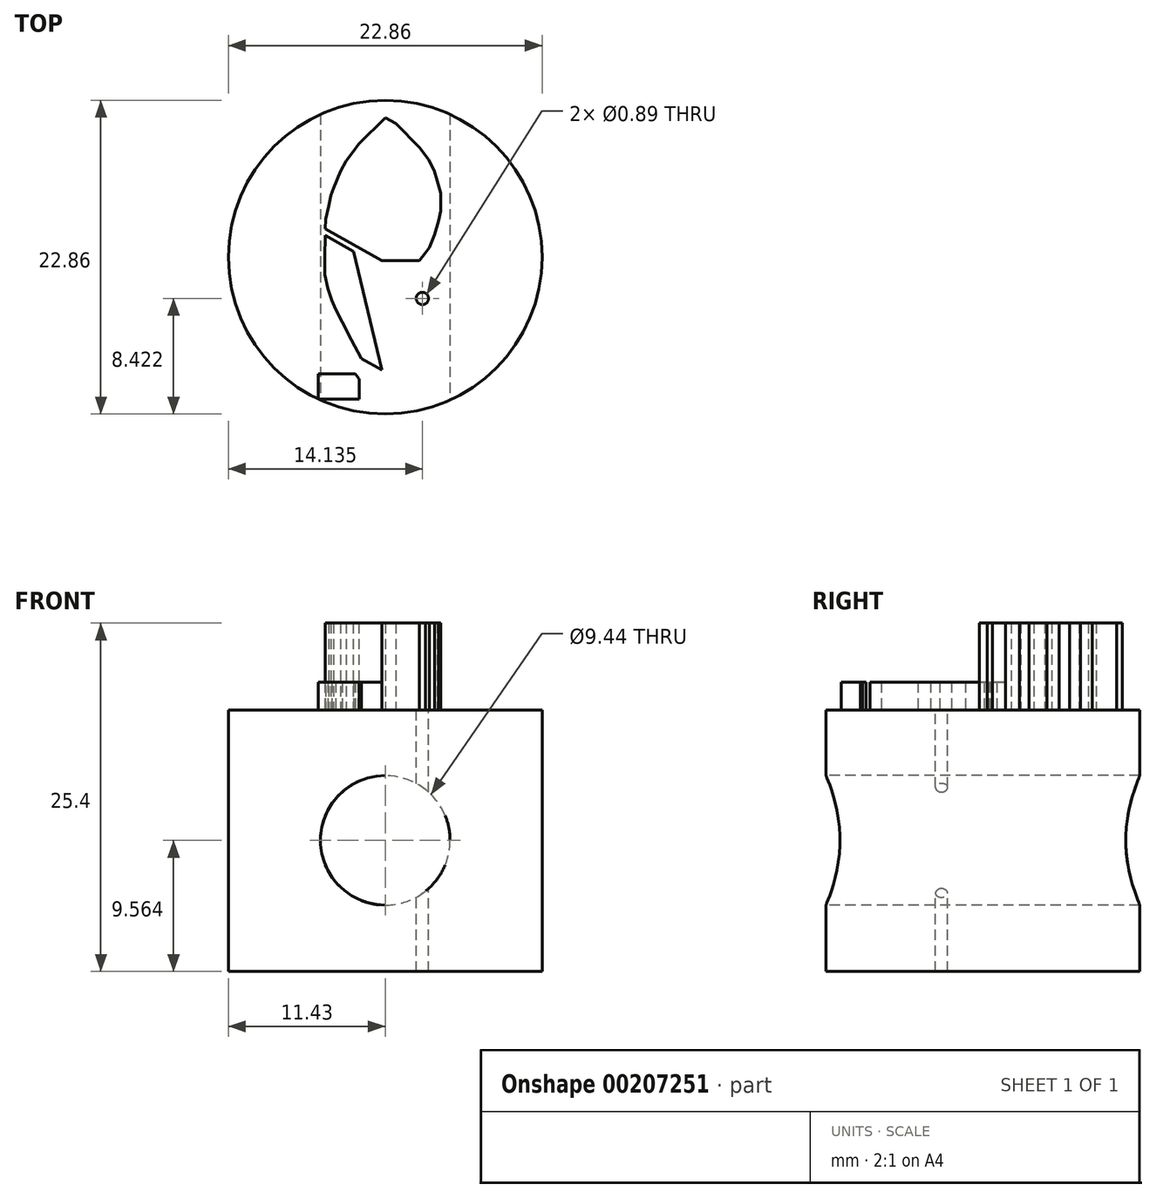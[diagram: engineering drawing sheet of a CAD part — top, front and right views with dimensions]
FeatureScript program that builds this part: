
annotation { "Feature Type Name" : "Feature", "Feature Type Description" : "" }
export const myFeature = defineFeature(function(context is Context, id is Id, definition is map)
    precondition{}
    {
        {
            var Q0;
            Q0=qCreatedBy(makeId("Top.planeOp"),FACE);
            var sketch = newSketch(context, id + "F0", { "sketchPlane" : qUnion([Q0])});
            skCircle(sketch, "E0", {"center": v(0, 0) * mm, "radius": 11.43 * mm});
            skSolve(sketch);
        }
        {
            var Q0;
            Q0 = qSketchRegion(id + "F0", true);
            extrude(context, id + "F1", {"entities" : qUnion([Q0]), "depth" : 19.05 * mm});
        }
        {
            var Q0;
            Q0=makeQuery(id+"F1.opExtrude","CAP_FACE",FACE,{"disambiguationData":[OSD([sQuery(id+"F0.wireOp",EDGE,"E0")])],"isStart":false});
            var sketch = newSketch(context, id + "F2", { "sketchPlane" : qUnion([Q0])});
            skCircle(sketch, "E1", {"center": v(2.7, -3) * mm, "radius": 0.45 * mm});
            skSolve(sketch);
        }
        {
            var Q0;
            Q0 = qSketchRegion(id + "F2", true);
            extrude(context, id + "F3", {"entities" : qUnion([Q0]), "operationType" : NewBodyOperationType.REMOVE, "oppositeDirection" : true, "depth" : 19.06 * mm});
        }
        {
            var Q0;
            Q0=makeQuery(id+"F1.opExtrude","CAP_FACE",FACE,{"disambiguationData":[OSD([sQuery(id+"F0.wireOp",EDGE,"E0")])],"isStart":false});
            var sketch = newSketch(context, id + "F4", { "sketchPlane" : qUnion([Q0])});
            skLineSegment(sketch, "E2", {"start": v(-2.18, -8.51) * mm, "end": v(-1.98, -8.77) * mm});
            skLineSegment(sketch, "E3", {"start": v(-1.98, -8.77) * mm, "end": v(-1.93, -8.85) * mm});
            skLineSegment(sketch, "E4", {"start": v(-1.93, -8.85) * mm, "end": v(-1.88, -8.92) * mm});
            skLineSegment(sketch, "E5", {"start": v(-1.88, -8.92) * mm, "end": v(-1.88, -9.2) * mm});
            skLineSegment(sketch, "E6", {"start": v(-1.88, -9.2) * mm, "end": v(-1.88, -9.88) * mm});
            skLineSegment(sketch, "E7", {"start": v(-1.88, -9.88) * mm, "end": v(-1.88, -10.33) * mm});
            skLineSegment(sketch, "E8", {"start": v(-4.89, -10.33) * mm, "end": v(-4.89, -8.51) * mm});
            skLineSegment(sketch, "E9", {"start": v(-4.89, -8.51) * mm, "end": v(-2.18, -8.51) * mm});
            skLineSegment(sketch, "E10", {"start": v(-4.89, -10.33) * mm, "end": v(-1.88, -10.33) * mm});
            skSolve(sketch);
        }
        {
            var Q0;
            Q0 = qSketchRegion(id + "F4", true);
            extrude(context, id + "F5", {"entities" : qUnion([Q0]), "operationType" : NewBodyOperationType.ADD, "depth" : 2.03 * mm});
        }
        {
            var Q0;
            Q0=makeQuery(id+"F1.opExtrude","CAP_FACE",FACE,{"disambiguationData":[OSD([sQuery(id+"F0.wireOp",EDGE,"E0")])],"isStart":false});
            var sketch = newSketch(context, id + "F6", { "sketchPlane" : qUnion([Q0])});
            skLineSegment(sketch, "E11", {"start": v(4.03, 3.8) * mm, "end": v(4.03, 4.68) * mm});
            skLineSegment(sketch, "E12", {"start": v(4.03, 4.68) * mm, "end": v(3.8, 5.57) * mm});
            skLineSegment(sketch, "E13", {"start": v(3.8, 5.57) * mm, "end": v(3.57, 6.33) * mm});
            skLineSegment(sketch, "E14", {"start": v(3.57, 6.33) * mm, "end": v(3.15, 7.12) * mm});
            skLineSegment(sketch, "E15", {"start": v(3.15, 7.12) * mm, "end": v(2.5, 7.98) * mm});
            skLineSegment(sketch, "E16", {"start": v(2.5, 7.98) * mm, "end": v(1.66, 8.85) * mm});
            skLineSegment(sketch, "E17", {"start": v(1.66, 8.85) * mm, "end": v(1.2, 9.32) * mm});
            skLineSegment(sketch, "E18", {"start": v(1.2, 9.32) * mm, "end": v(0.78, 9.74) * mm});
            skLineSegment(sketch, "E19", {"start": v(0.78, 9.74) * mm, "end": v(0, 10.16) * mm});
            skLineSegment(sketch, "E20", {"start": v(0, 10.16) * mm, "end": v(-0.6, 9.56) * mm});
            skLineSegment(sketch, "E21", {"start": v(-0.6, 9.56) * mm, "end": v(-1.34, 8.85) * mm});
            skLineSegment(sketch, "E22", {"start": v(-1.34, 8.85) * mm, "end": v(-1.94, 8.26) * mm});
            skLineSegment(sketch, "E23", {"start": v(-1.94, 8.26) * mm, "end": v(-2.33, 7.68) * mm});
            skLineSegment(sketch, "E24", {"start": v(-3.15, -4.72) * mm, "end": v(-2.46, -6.03) * mm});
            skLineSegment(sketch, "E25", {"start": v(-2.46, -6.03) * mm, "end": v(-1.74, -7.4) * mm});
            skLineSegment(sketch, "E26", {"start": v(-1.74, -7.4) * mm, "end": v(-0.24, -8.21) * mm});
            skLineSegment(sketch, "E27", {"start": v(-4.38, 1.01) * mm, "end": v(-4.38, 1.57) * mm});
            skLineSegment(sketch, "E28", {"start": v(-4.1, 3.71) * mm, "end": v(-3.95, 4.5) * mm});
            skLineSegment(sketch, "E29", {"start": v(-3.95, 4.5) * mm, "end": v(-3.76, 5) * mm});
            skLineSegment(sketch, "E30", {"start": v(-3.76, 5) * mm, "end": v(-3.27, 6.25) * mm});
            skLineSegment(sketch, "E31", {"start": v(-3.27, 6.25) * mm, "end": v(-2.84, 7.02) * mm});
            skLineSegment(sketch, "E32", {"start": v(-2.84, 7.02) * mm, "end": v(-2.33, 7.68) * mm});
            skLineSegment(sketch, "E33", {"start": v(-4.38, 2.07) * mm, "end": v(-4.34, 2.75) * mm});
            skLineSegment(sketch, "E34", {"start": v(-4.34, 2.75) * mm, "end": v(-4.1, 3.71) * mm});
            skLineSegment(sketch, "E35", {"start": v(-4.42, -0.55) * mm, "end": v(-4.42, 0.1) * mm});
            skLineSegment(sketch, "E36", {"start": v(-4.42, 0.1) * mm, "end": v(-4.4, 0.53) * mm});
            skLineSegment(sketch, "E37", {"start": v(-4.4, 0.53) * mm, "end": v(-4.38, 1.01) * mm});
            skLineSegment(sketch, "E38", {"start": v(-3.15, -4.72) * mm, "end": v(-3.6, -3.81) * mm});
            skLineSegment(sketch, "E39", {"start": v(-3.6, -3.81) * mm, "end": v(-3.9, -3.14) * mm});
            skLineSegment(sketch, "E40", {"start": v(-3.9, -3.14) * mm, "end": v(-4.18, -2.3) * mm});
            skLineSegment(sketch, "E41", {"start": v(-4.18, -2.3) * mm, "end": v(-4.42, -1.27) * mm});
            skLineSegment(sketch, "E42", {"start": v(-4.42, -1.27) * mm, "end": v(-4.42, -0.55) * mm});
            skLineSegment(sketch, "E43", {"start": v(2.48, -0.25) * mm, "end": v(2.94, 0.3) * mm});
            skLineSegment(sketch, "E44", {"start": v(2.94, 0.3) * mm, "end": v(3.2, 0.7) * mm});
            skLineSegment(sketch, "E45", {"start": v(3.2, 0.7) * mm, "end": v(3.41, 1.19) * mm});
            skLineSegment(sketch, "E46", {"start": v(3.41, 1.19) * mm, "end": v(3.61, 1.66) * mm});
            skLineSegment(sketch, "E47", {"start": v(3.61, 1.66) * mm, "end": v(3.74, 2.14) * mm});
            skLineSegment(sketch, "E48", {"start": v(3.74, 2.14) * mm, "end": v(3.89, 2.65) * mm});
            skLineSegment(sketch, "E49", {"start": v(3.89, 2.65) * mm, "end": v(4.03, 3.38) * mm});
            skLineSegment(sketch, "E50", {"start": v(4.03, 3.8) * mm, "end": v(4.03, 3.38) * mm});
            skLineSegment(sketch, "E51", {"start": v(2.48, -0.25) * mm, "end": v(-0.24, -0.25) * mm});
            skLineSegment(sketch, "E52", {"start": v(-0.24, -0.25) * mm, "end": v(-4.38, 2.07) * mm});
            skLineSegment(sketch, "E53", {"start": v(-2.31, 0.4) * mm, "end": v(-0.24, -8.21) * mm});
            skLineSegment(sketch, "E54", {"start": v(-4.38, 1.57) * mm, "end": v(-2.31, 0.4) * mm});
            skSolve(sketch);
        }
        {
            var Q0;
            Q0=qCreatedBy(makeId("Front.planeOp"),FACE);
            var sketch = newSketch(context, id + "F7", { "sketchPlane" : qUnion([Q0])});
            skCircle(sketch, "E55", {"center": v(0, 9.56) * mm, "radius": 4.72 * mm});
            skSolve(sketch);
        }
        {
            var Q0;
            Q0 = qSketchRegion(id + "F7", true);
            extrude(context, id + "F8", {"entities" : qUnion([Q0]), "operationType" : NewBodyOperationType.REMOVE, "oppositeDirection" : true, "depth" : 13.6 * mm});
        }
        {
            var Q0;
            Q0 = qSketchRegion(id + "F7", true);
            extrude(context, id + "F9", {"entities" : qUnion([Q0]), "operationType" : NewBodyOperationType.REMOVE, "depth" : 12.42 * mm});
        }
        {
            var Q0;
            Q0=makeQuery(id+"F6.imprint","IMPRINT",FACE,{"disambiguationData":[TD([[makeQuery(id+"F6.imprint","IMPRINT",EDGE,{"derivedFrom":sQuery(id+"F6.wireOp",EDGE,"E11")}),1.0]])]});
            extrude(context, id + "F10", {"entities" : qUnion([Q0]), "operationType" : NewBodyOperationType.ADD, "depth" : 6.35 * mm});
        }
        {
            var Q0;
            Q0=makeQuery(id+"F6.imprint","IMPRINT",FACE,{"disambiguationData":[TD([[makeQuery(id+"F6.imprint","IMPRINT",EDGE,{"derivedFrom":sQuery(id+"F6.wireOp",EDGE,"E24")}),1.0]])]});
            extrude(context, id + "F11", {"entities" : qUnion([Q0]), "operationType" : NewBodyOperationType.ADD, "depth" : 2.03 * mm});
        }
    });
